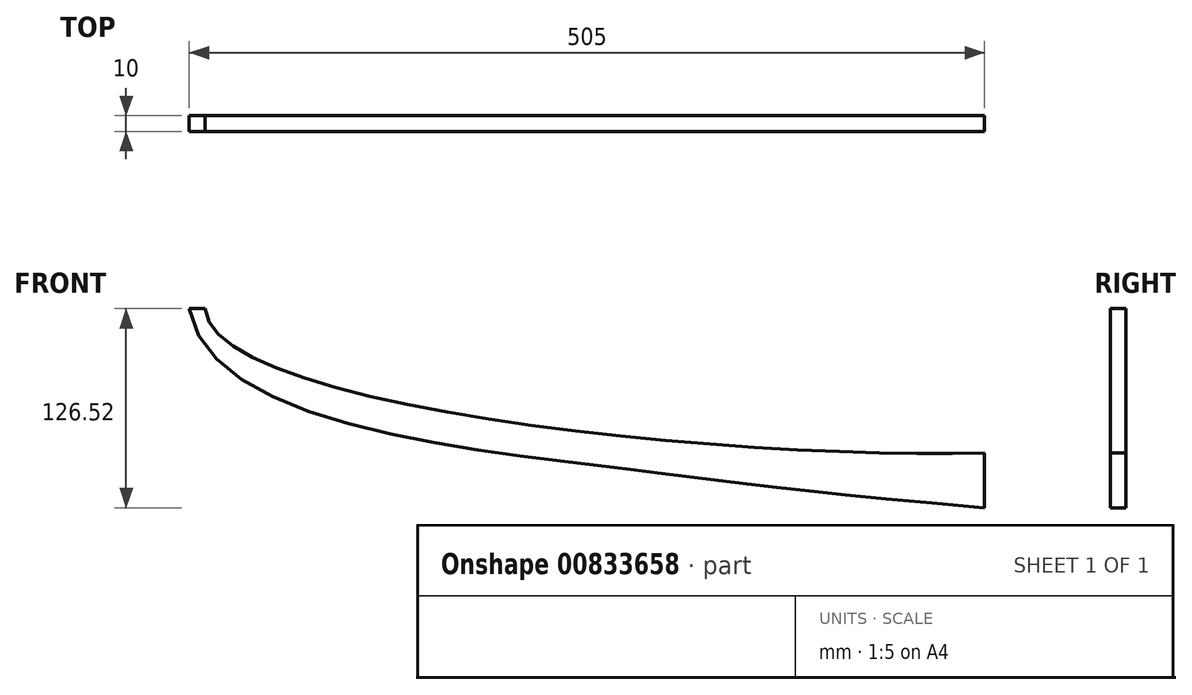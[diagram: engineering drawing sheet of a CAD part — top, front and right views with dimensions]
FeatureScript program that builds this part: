
annotation { "Feature Type Name" : "Feature", "Feature Type Description" : "" }
export const myFeature = defineFeature(function(context is Context, id is Id, definition is map)
    precondition{}
    {
        {
            var Q0;
            Q0=qCreatedBy(makeId("Front.planeOp"),FACE);
            var sketch = newSketch(context, id + "F0", { "sketchPlane" : qUnion([Q0])});
            skLineSegment(sketch, "E0", {"start": v(-21.6, 0) * mm, "end": v(-11.6, 0) * mm});
            skFitSpline(sketch, "E1", {"points": [v(-11.6, 0) * mm, v(483.4, -91.6) * mm], "startDerivative": vector(13.8, -196.65) * mm, "endDerivative": vector(444.63, 14.01) * mm});
            skLineSegment(sketch, "E2", {"start": v(483.4, -91.6) * mm, "end": v(483.4, -126.52) * mm});
            skLineSegment(sketch, "E3", {"start": v(483.4, -91.6) * mm, "end": v(483.4, 0) * mm});
            skFitSpline(sketch, "E4", {"points": [v(-21.6, 0) * mm, v(229.95, -98.64) * mm, v(483.4, -126.52) * mm], "startDerivative": vector(71.87, -420.6) * mm, "endDerivative": vector(822.43, -71.87) * mm});
            skSolve(sketch);
        }
        {
            var Q0;
            {var subQ0=sQuery(id+"F0.wireOp",EDGE,"E0");Q0=makeQuery(id+"F0.imprint","IMPRINT",FACE,{"disambiguationData":[TD([[makeQuery(id+"F0.imprint","IMPRINT",EDGE,{"derivedFrom":subQ0}),-1.0]])]});}
            extrude(context, id + "F1", {"entities" : qUnion([Q0]), "depth" : 10 * mm, "offsetDistance" : 25 * mm});
        }
    });
